# Revit family: 447801 SENTINEL KINETIC 300Z
name_source: partatom
category: Mechanical Equipment
revit_build: Autodesk Revit MEP 2013 (Build: 20120221_2030(x64)
units: mm (PartAtom-declared; Revit-internal decimal feet)

## types (2) — shared parameters
AC Frequency Input = 50Hz nominal
AC Voltage Input = 220-240 V AC (single phase)
Category = Sentinel Kinetic
Condensate Pipe Diameter = 22 mm  [stored 0.0721785 ft]
Family = Kinetic
Height (excluding Spigots) = 301 mm  [stored 0.987533 ft]
IP Rating = IP22
Length (excluding spigots) = 940 mm  [stored 3.08399 ft]
Length (including Spigots) = 985 mm  [stored 3.23163 ft]
Manufacturer - Name = Vent-Axia Ltd
Manufacturer - Website = www.vent-axia.com
Motor Rating = 150 Watts (max)
Operating Humidity = 0% to 95% RH
Operating Temperature = (-10C to +40C)
Operational and Maintenance Manual = http://www.vent-axia.com
Spigot Diameter = 150 mm  [stored 0.492126 ft]
Warranty period = Unit 2 Years , Motor 5 Years
Weight = 38kg
Width (excluding Spigots) = 720 mm  [stored 2.3622 ft]

## per-type parameters (varying)
| type | Part Number | Product Description |
| 300ZH | 449536 | Kinetic 300Z Horizontal wth Humidity Sensor |
| 300Z | 447801 | Kinetic 300Z Horizontal |

note: column(s) folded — value = type name in every type: Sub Type

note: [stored X ft] marks values corroborated as IEEE doubles in the binary element streams (Revit-internal decimal feet)

## geometry (parser evidence)
native form markers: Sweep x1
no freeform markers — native parametric forms only
